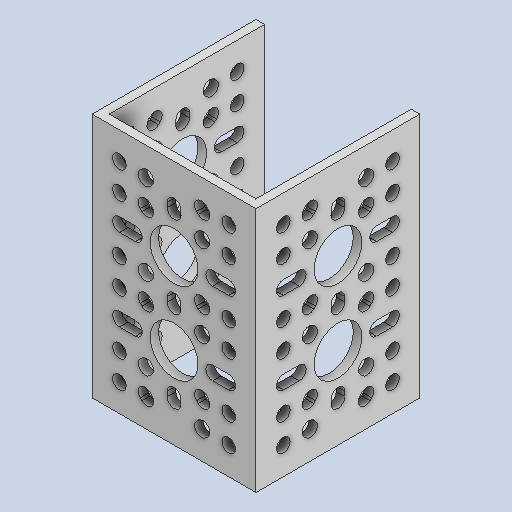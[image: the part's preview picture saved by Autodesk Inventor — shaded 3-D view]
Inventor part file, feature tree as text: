
AUTODESK INVENTOR PART (.ipt)
format: ipt  version: 2023 (Build 270158000, 158)  size: 506,368 bytes
history: native  units: in
note: dims shown in document units (in); Inventor stores cm internally (conversion verified against a paired STEP export)
features: mirror x1
ambient origin geometry x8: Origin, YZ Plane, XZ Plane, XY Plane, X Axis, Y Axis, Z Axis, Center Point
bodies: Solid1 (feature_tree)
feature tree (1):
  mirror  "Mirror5"
